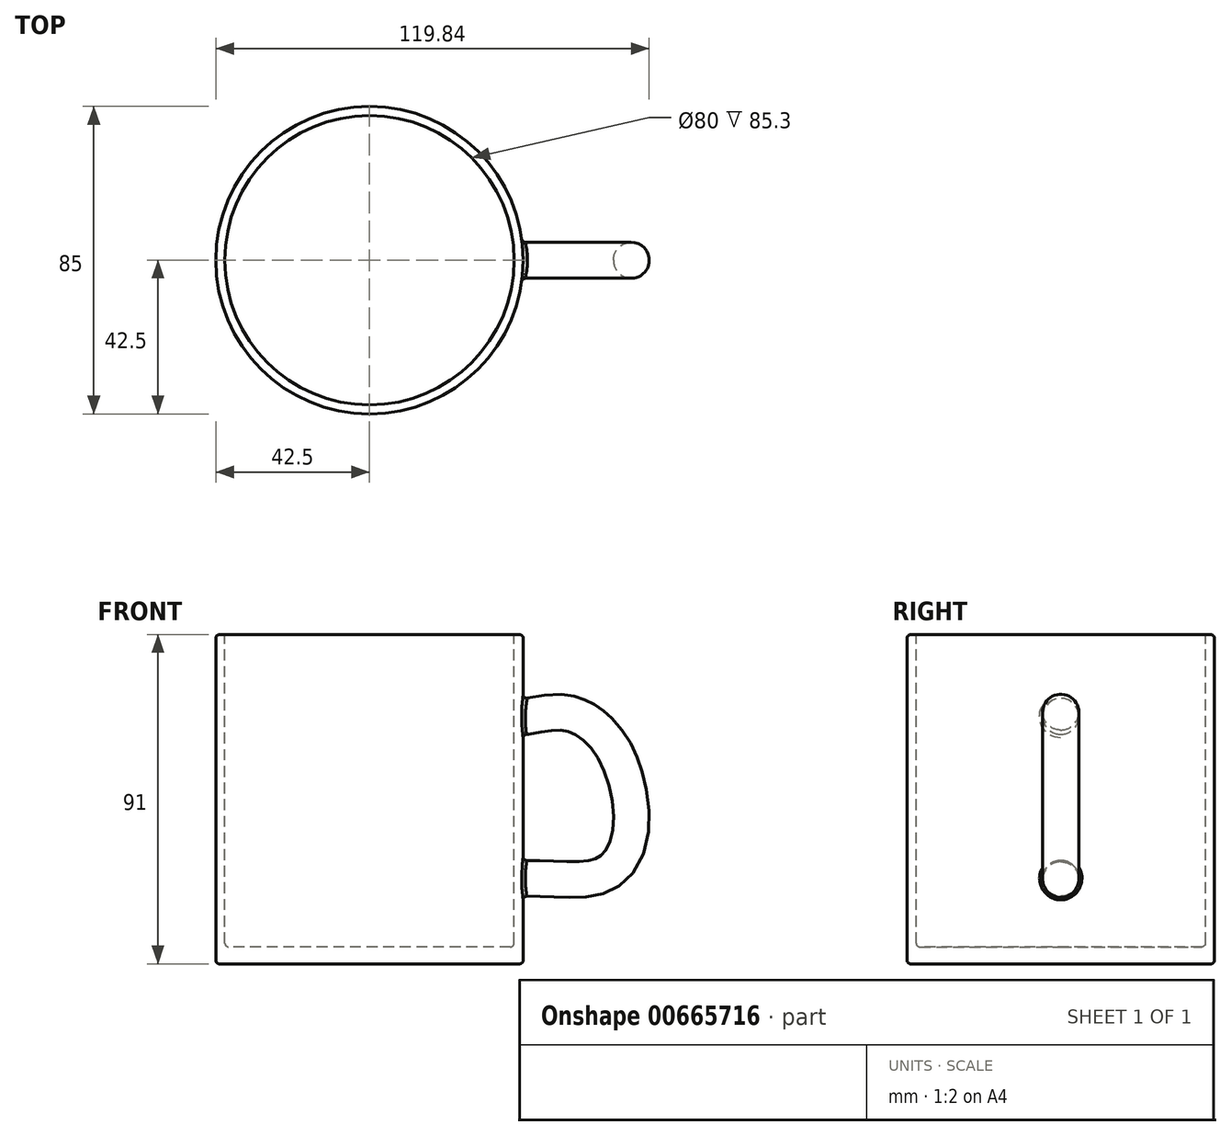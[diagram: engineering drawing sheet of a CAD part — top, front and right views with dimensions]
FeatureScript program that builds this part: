
annotation { "Feature Type Name" : "Feature", "Feature Type Description" : "" }
export const myFeature = defineFeature(function(context is Context, id is Id, definition is map)
    precondition{}
    {
        {
            var Q0;
            Q0=qCreatedBy(makeId("Top.planeOp"),FACE);
            var sketch = newSketch(context, id + "F0", { "sketchPlane" : qUnion([Q0])});
            skCircle(sketch, "E0", {"center": v(0, 0) * mm, "radius": 42.5 * mm});
            skSolve(sketch);
        }
        {
            var Q0;
            Q0=makeQuery(id+"F0.imprint","IMPRINT",FACE,{"disambiguationData":[TD([[makeQuery(id+"F0.imprint","IMPRINT",EDGE,{"derivedFrom":sQuery(id+"F0.wireOp",EDGE,"E0")}),1.0]])]});
            extrude(context, id + "F1", {"entities" : qUnion([Q0]), "depth" : 91 * mm, "offsetDistance" : 25 * mm});
        }
        {
            var Q0;
            Q0=qCreatedBy(makeId("Front.planeOp"),FACE);
            var sketch = newSketch(context, id + "F2", { "sketchPlane" : qUnion([Q0])});
            skFitSpline(sketch, "E1", {"points": [v(37.75, 70.09) * mm, v(42.95, 69.46) * mm, v(53.97, 70.5) * mm, v(67.7, 60.93) * mm, v(73.11, 35.56) * mm, v(65, 23.7) * mm, v(48.98, 22.46) * mm, v(36.92, 22.46) * mm], "startDerivative": vector(53.84, -13.1) * mm, "endDerivative": vector(-84.9, -1.99) * mm});
            skSolve(sketch);
        }
        {
            var Q0;
            Q0=qCreatedBy(makeId("Right.planeOp"),FACE);
            cPlane(context, id + "F3", {"entities" : qUnion([Q0]), "cplaneType" : CPlaneType.OFFSET, "offset" : 40 * mm, "width" : 150 * mm, "height" : 150 * mm});
        }
        {
            var Q0;
            Q0=qCreatedBy(id+"F3.planeOp",FACE);
            var sketch = newSketch(context, id + "F4", { "sketchPlane" : qUnion([Q0])});
            skCircle(sketch, "E2", {"center": v(0, 68.52) * mm, "radius": 5 * mm});
            skSolve(sketch);
        }
        {
            var Q0;
            Q0 = qSketchRegion(id + "F4", true);
            var Q1;
            Q1=sQuery(id+"F2.wireOp",EDGE,"E1");
            sweep(context, id + "F5", {"operationType" : NewBodyOperationType.ADD, "profiles" : qUnion([Q0]), "path" : qUnion([Q1])});
        }
        {
            var Q0;
            Q0=makeQuery(id+"F1.opExtrude","CAP_FACE",FACE,{"disambiguationData":[OSD([sQuery(id+"F0.wireOp",EDGE,"E0")])],"isStart":false});
            cPlane(context, id + "F6", {"entities" : qUnion([Q0]), "cplaneType" : CPlaneType.OFFSET, "offset" : 0 * mm, "width" : 150 * mm, "height" : 150 * mm});
        }
        {
            var Q0;
            Q0=qCreatedBy(id+"F6.planeOp",FACE);
            var sketch = newSketch(context, id + "F7", { "sketchPlane" : qUnion([Q0])});
            skCircle(sketch, "E3", {"center": v(0, 0) * mm, "radius": 40 * mm});
            skSolve(sketch);
        }
        {
            var Q0;
            Q0 = qSketchRegion(id + "F7", true);
            extrude(context, id + "F8", {"entities" : qUnion([Q0]), "operationType" : NewBodyOperationType.REMOVE, "oppositeDirection" : true, "depth" : 86.3 * mm, "offsetDistance" : 25 * mm});
        }
        {
            var Q0;
            Q0=makeQuery(id+"F1.opExtrude","CAP_EDGE",EDGE,{"disambiguationData":[OSD([sQuery(id+"F0.wireOp",EDGE,"E0")])],"isStart":false});
            var Q1;
            Q1=makeQuery(id+"F8.boolean.opBoolean","COPY",EDGE,{"derivedFrom":makeQuery(id+"F8.opExtrude","CAP_EDGE",EDGE,{"disambiguationData":[OSD([sQuery(id+"F7.wireOp",EDGE,"E3")])],"isStart":true})});
            var Q2;
            Q2=makeQuery(id+"F8.boolean.opBoolean","COPY",EDGE,{"derivedFrom":makeQuery(id+"F8.opExtrude","CAP_EDGE",EDGE,{"disambiguationData":[OSD([sQuery(id+"F7.wireOp",EDGE,"E3")])],"isStart":false})});
            var Q3;
            Q3=makeQuery(id+"F1.opExtrude","CAP_EDGE",EDGE,{"disambiguationData":[OSD([sQuery(id+"F0.wireOp",EDGE,"E0")])],"isStart":true});
            var Q4;
            Q4=makeQuery(id+"F5.opSweep","SWEPT_FACE",FACE,{"disambiguationData":[OSD([sQuery(id+"F2.wireOp",EDGE,"E1"),sQuery(id+"F4.wireOp",EDGE,"E2")])]});
            fillet(context, id + "F9", {"entities" : qUnion([Q0, Q1, Q2, Q3, Q4]), "radius" : 1 * mm, "tangentPropagation" : true, "allowEdgeOverflow" : false});
        }
    });
